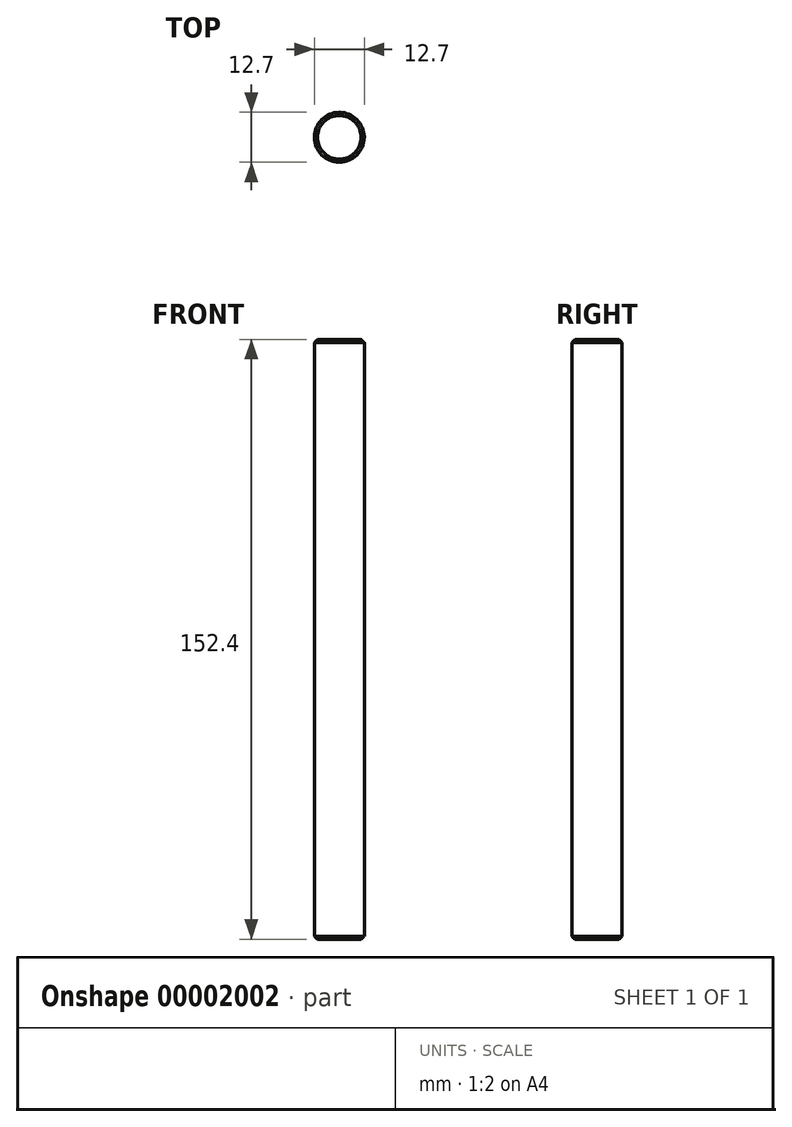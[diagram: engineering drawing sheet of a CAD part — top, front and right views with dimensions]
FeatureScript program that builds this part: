
annotation { "Feature Type Name" : "Feature", "Feature Type Description" : "" }
export const myFeature = defineFeature(function(context is Context, id is Id, definition is map)
    precondition{}
    {
        {
            var Q0;
            Q0=qCreatedBy(makeId("Top.planeOp"),FACE);
            var sketch = newSketch(context, id + "F0", { "sketchPlane" : qUnion([Q0])});
            skCircle(sketch, "E0", {"center": v(0, 0) * mm, "radius": 6.35 * mm});
            skSolve(sketch);
        }
        {
            var Q0;
            Q0=qSketchRegion(id+"F0",true);
            extrude(context, id + "F1", {"entities" : qUnion([Q0]), "depth" : 76.2 * mm});
        }
        {
            var Q0;
            Q0=qSketchRegion(id+"F0",true);
            extrude(context, id + "F2", {"entities" : qUnion([Q0]), "operationType" : NewBodyOperationType.ADD, "oppositeDirection" : true, "depth" : 76.2 * mm});
        }
        {
            var Q0;
            Q0=makeQuery(id+"F1.opExtrude","CAP_EDGE",EDGE,{"disambiguationData":[OSD([sQuery(id+"F0.wireOp",EDGE,"E0")])],"isStart":false});
            var Q1;
            Q1=makeQuery(id+"F2.opExtrude","CAP_EDGE",EDGE,{"disambiguationData":[OSD([sQuery(id+"F0.wireOp",EDGE,"E0")])],"isStart":false});
            chamfer(context, id + "F3", {"entities" : qUnion([Q0, Q1]), "width" : 0.79 * mm, "tangentPropagation" : true});
        }
    });
